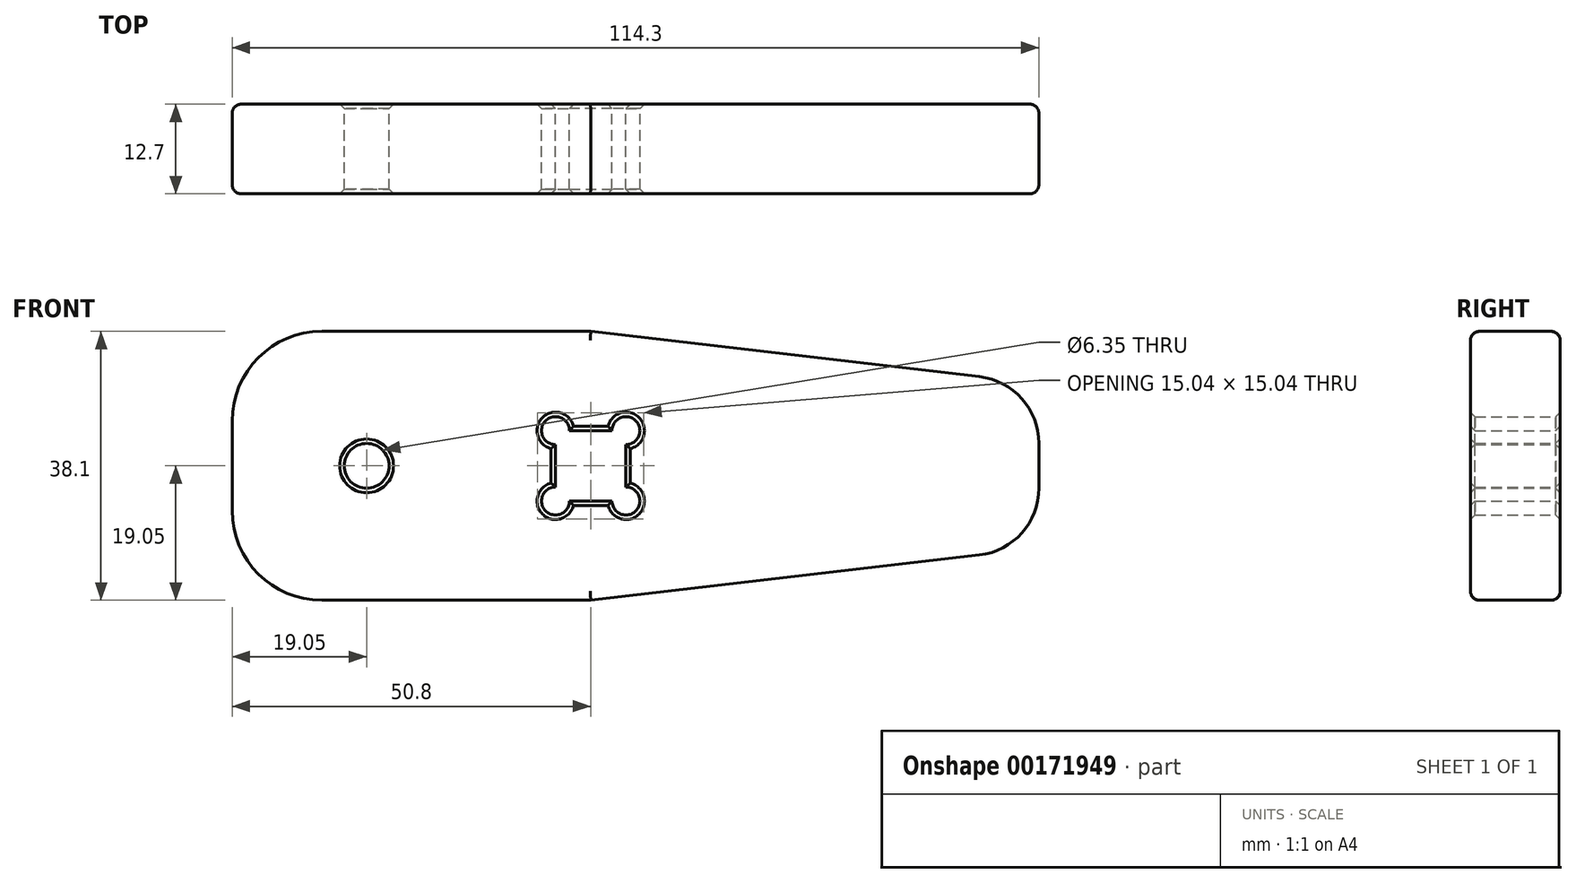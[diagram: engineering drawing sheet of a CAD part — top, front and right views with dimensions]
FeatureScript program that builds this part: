
annotation { "Feature Type Name" : "Feature", "Feature Type Description" : "" }
export const myFeature = defineFeature(function(context is Context, id is Id, definition is map)
    precondition{}
    {
        {
            var Q0;
            Q0=qCreatedBy(makeId("Front.planeOp"),FACE);
            var sketch = newSketch(context, id + "F0", { "sketchPlane" : qUnion([Q0])});
            skLineSegment(sketch, "E0.bottom", {"start": v(3, -5) * mm, "end": v(-3, -5) * mm});
            skLineSegment(sketch, "E0.top", {"start": v(3, 5) * mm, "end": v(-3, 5) * mm});
            skLineSegment(sketch, "E0.left", {"start": v(5, -3) * mm, "end": v(5, 3) * mm});
            skLineSegment(sketch, "E0.right", {"start": v(-5, -3) * mm, "end": v(-5, 3) * mm});
            skPoint(sketch, "E0.middle", {"position": v(0, 0) * mm});
            skCircle(sketch, "E1", {"center": v(-31.75, 0) * mm, "radius": 3.18 * mm});
            skArc(sketch, "E2", {"start": v(-3, 5) * mm, "mid": v(-6.4, 6.4) * mm, "end": v(-5, 3) * mm});
            skArc(sketch, "E3.MirrorC", {"start": v(3, 5) * mm, "mid": v(6.4, 6.4) * mm, "end": v(5, 3) * mm});
            skArc(sketch, "E4.MirrorC", {"start": v(3, -5) * mm, "mid": v(6.4, -6.4) * mm, "end": v(5, -3) * mm});
            skArc(sketch, "E5.MirrorC", {"start": v(-3, -5) * mm, "mid": v(-6.4, -6.4) * mm, "end": v(-5, -3) * mm});
            skLineSegment(sketch, "E6.bottom", {"start": v(0, -19.05) * mm, "end": v(-38.1, -19.05) * mm});
            skArc(sketch, "E7", {"start": v(55.08, -12.64) * mm, "mid": v(61.09, -9.5) * mm, "end": v(63.5, -3.17) * mm});
            skLineSegment(sketch, "E8", {"start": v(0, -19.05) * mm, "end": v(55.08, -12.64) * mm});
            skArc(sketch, "E9", {"start": v(-50.8, -6.35) * mm, "mid": v(-47.08, -15.33) * mm, "end": v(-38.1, -19.05) * mm});
            skArc(sketch, "E10.MirrorCS", {"start": v(55.08, 12.64) * mm, "mid": v(61.09, 9.5) * mm, "end": v(63.5, 3.17) * mm});
            skLineSegment(sketch, "E11.MirrorCS", {"start": v(0, 19.05) * mm, "end": v(55.08, 12.64) * mm});
            skLineSegment(sketch, "E12.MirrorCS", {"start": v(0, 19.05) * mm, "end": v(-38.1, 19.05) * mm});
            skArc(sketch, "E13.MirrorCS", {"start": v(-50.8, 6.35) * mm, "mid": v(-47.08, 15.33) * mm, "end": v(-38.1, 19.05) * mm});
            skLineSegment(sketch, "E14", {"start": v(63.5, 3.17) * mm, "end": v(63.5, -3.17) * mm});
            skLineSegment(sketch, "E15", {"start": v(-50.8, 6.35) * mm, "end": v(-50.8, -6.35) * mm});
            skSolve(sketch);
        }
        {
            var Q0;
            Q0 = qSketchRegion(id + "F0", true);
            extrude(context, id + "F1", {"entities" : qUnion([Q0]), "depth" : 12.7 * mm});
        }
        {
            var Q0;
            Q0=makeQuery(id+"F1.opExtrude","CAP_EDGE",EDGE,{"disambiguationData":[OSD([sQuery(id+"F0.wireOp",EDGE,"E12.MirrorCS")])],"isStart":false});
            var Q1;
            Q1=makeQuery(id+"F1.opExtrude","CAP_EDGE",EDGE,{"disambiguationData":[OSD([sQuery(id+"F0.wireOp",EDGE,"E11.MirrorCS")])],"isStart":false});
            var Q2;
            Q2=makeQuery(id+"F1.opExtrude","CAP_EDGE",EDGE,{"disambiguationData":[OSD([sQuery(id+"F0.wireOp",EDGE,"E12.MirrorCS")])],"isStart":true});
            var Q3;
            Q3=makeQuery(id+"F1.opExtrude","CAP_EDGE",EDGE,{"disambiguationData":[OSD([sQuery(id+"F0.wireOp",EDGE,"E11.MirrorCS")])],"isStart":true});
            fillet(context, id + "F2", {"entities" : qUnion([Q0, Q1, Q2, Q3]), "radius" : 1.27 * mm, "tangentPropagation" : true, "allowEdgeOverflow" : false});
        }
        {
            var Q0;
            Q0=makeQuery(id+"F1.opExtrude","CAP_EDGE",EDGE,{"disambiguationData":[OSD([sQuery(id+"F0.wireOp",EDGE,"E1")])],"isStart":false});
            var Q1;
            Q1=makeQuery(id+"F1.opExtrude","CAP_EDGE",EDGE,{"disambiguationData":[OSD([sQuery(id+"F0.wireOp",EDGE,"E0.right")])],"isStart":false});
            var Q2;
            Q2=makeQuery(id+"F1.opExtrude","CAP_EDGE",EDGE,{"disambiguationData":[OSD([sQuery(id+"F0.wireOp",EDGE,"E0.top")])],"isStart":false});
            var Q3;
            Q3=makeQuery(id+"F1.opExtrude","CAP_EDGE",EDGE,{"disambiguationData":[OSD([sQuery(id+"F0.wireOp",EDGE,"E0.left")])],"isStart":false});
            var Q4;
            Q4=makeQuery(id+"F1.opExtrude","CAP_EDGE",EDGE,{"disambiguationData":[OSD([sQuery(id+"F0.wireOp",EDGE,"E0.bottom")])],"isStart":false});
            var Q5;
            Q5=makeQuery(id+"F1.opExtrude","CAP_EDGE",EDGE,{"disambiguationData":[OSD([sQuery(id+"F0.wireOp",EDGE,"E4.MirrorC")])],"isStart":false});
            var Q6;
            Q6=makeQuery(id+"F1.opExtrude","CAP_EDGE",EDGE,{"disambiguationData":[OSD([sQuery(id+"F0.wireOp",EDGE,"E5.MirrorC")])],"isStart":false});
            var Q7;
            Q7=makeQuery(id+"F1.opExtrude","CAP_EDGE",EDGE,{"disambiguationData":[OSD([sQuery(id+"F0.wireOp",EDGE,"E2")])],"isStart":false});
            var Q8;
            Q8=makeQuery(id+"F1.opExtrude","CAP_EDGE",EDGE,{"disambiguationData":[OSD([sQuery(id+"F0.wireOp",EDGE,"E3.MirrorC")])],"isStart":false});
            var Q9;
            Q9=makeQuery(id+"F1.opExtrude","CAP_EDGE",EDGE,{"disambiguationData":[OSD([sQuery(id+"F0.wireOp",EDGE,"E1")])],"isStart":true});
            var Q10;
            Q10=makeQuery(id+"F1.opExtrude","CAP_EDGE",EDGE,{"disambiguationData":[OSD([sQuery(id+"F0.wireOp",EDGE,"E0.right")])],"isStart":true});
            var Q11;
            Q11=makeQuery(id+"F1.opExtrude","CAP_EDGE",EDGE,{"disambiguationData":[OSD([sQuery(id+"F0.wireOp",EDGE,"E2")])],"isStart":true});
            var Q12;
            Q12=makeQuery(id+"F1.opExtrude","CAP_EDGE",EDGE,{"disambiguationData":[OSD([sQuery(id+"F0.wireOp",EDGE,"E0.top")])],"isStart":true});
            var Q13;
            Q13=makeQuery(id+"F1.opExtrude","CAP_EDGE",EDGE,{"disambiguationData":[OSD([sQuery(id+"F0.wireOp",EDGE,"E3.MirrorC")])],"isStart":true});
            var Q14;
            Q14=makeQuery(id+"F1.opExtrude","CAP_EDGE",EDGE,{"disambiguationData":[OSD([sQuery(id+"F0.wireOp",EDGE,"E0.left")])],"isStart":true});
            var Q15;
            Q15=makeQuery(id+"F1.opExtrude","CAP_EDGE",EDGE,{"disambiguationData":[OSD([sQuery(id+"F0.wireOp",EDGE,"E4.MirrorC")])],"isStart":true});
            var Q16;
            Q16=makeQuery(id+"F1.opExtrude","CAP_EDGE",EDGE,{"disambiguationData":[OSD([sQuery(id+"F0.wireOp",EDGE,"E0.bottom")])],"isStart":true});
            var Q17;
            Q17=makeQuery(id+"F1.opExtrude","CAP_EDGE",EDGE,{"disambiguationData":[OSD([sQuery(id+"F0.wireOp",EDGE,"E5.MirrorC")])],"isStart":true});
            chamfer(context, id + "F3", {"entities" : qUnion([Q0, Q1, Q2, Q3, Q4, Q5, Q6, Q7, Q8, Q9, Q10, Q11, Q12, Q13, Q14, Q15, Q16, Q17]), "width" : 0.64 * mm, "tangentPropagation" : true});
        }
    });
